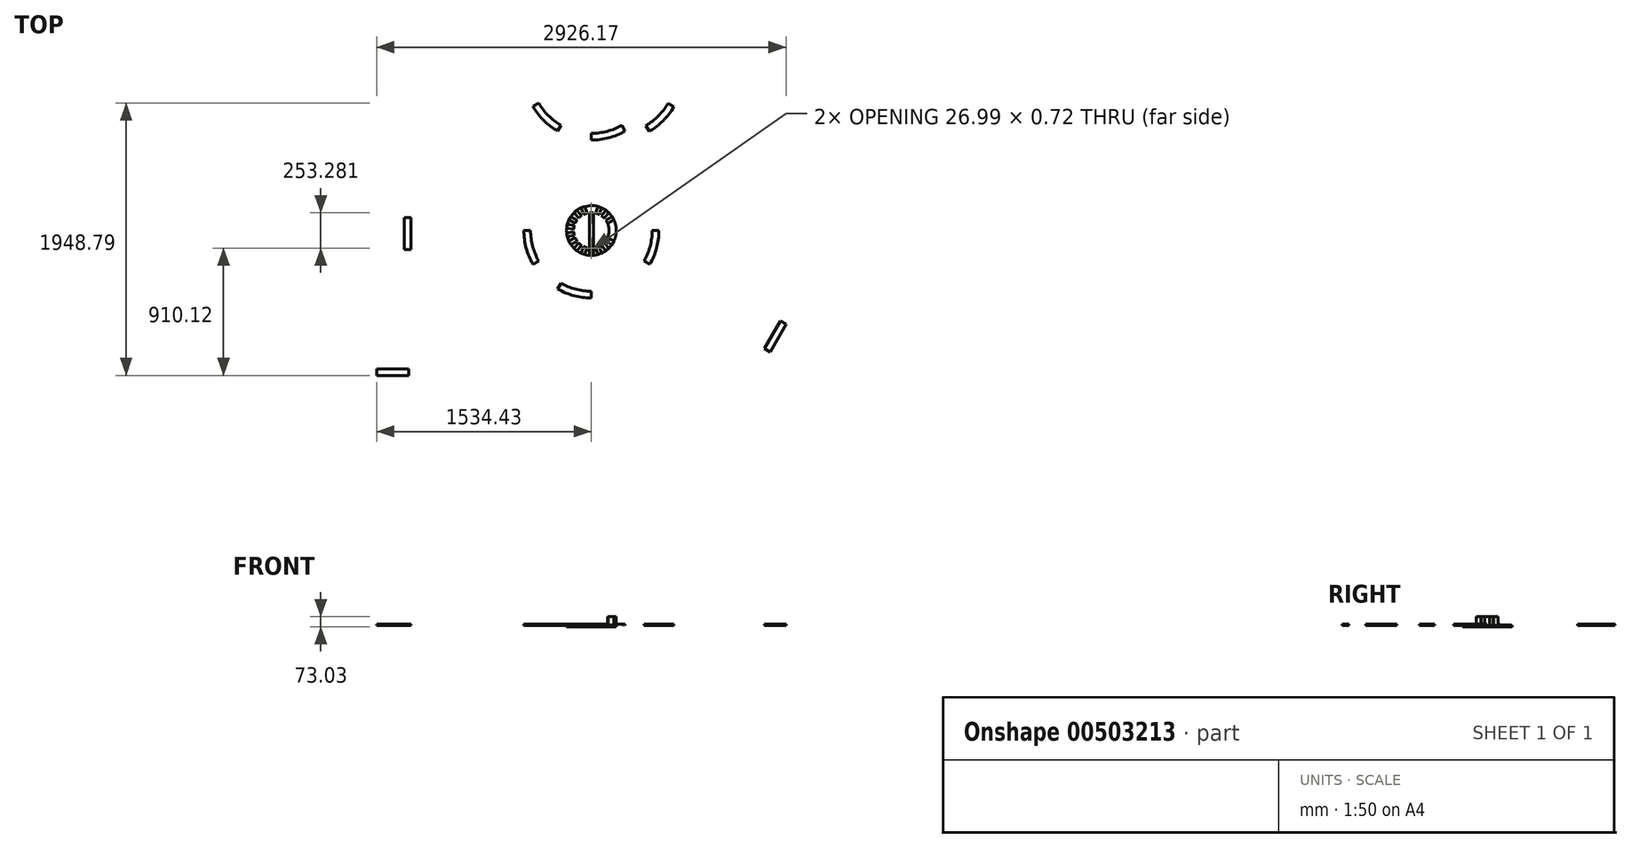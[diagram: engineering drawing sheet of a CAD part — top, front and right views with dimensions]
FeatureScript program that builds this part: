
annotation { "Feature Type Name" : "Feature", "Feature Type Description" : "" }
export const myFeature = defineFeature(function(context is Context, id is Id, definition is map)
    precondition{}
    {
        {
            var Q0;
            Q0=qCreatedBy(makeId("Top.planeOp"),FACE);
            var sketch = newSketch(context, id + "F0", { "sketchPlane" : qUnion([Q0])});
            skArc(sketch, "E0", {"start": v(-482.6, 0) * mm, "mid": v(-466.16, -124.9) * mm, "end": v(-417.94, -241.3) * mm});
            skArc(sketch, "E1.0", {"start": v(-434.98, 0) * mm, "mid": v(-420.15, -112.58) * mm, "end": v(-376.7, -217.49) * mm});
            skLineSegment(sketch, "E2", {"start": v(-482.6, 0) * mm, "end": v(-434.98, 0) * mm});
            skLineSegment(sketch, "E3", {"start": v(0, -434.98) * mm, "end": v(0, -482.6) * mm});
            skLineSegment(sketch, "E4", {"start": v(-376.7, -217.49) * mm, "end": v(-417.94, -241.3) * mm});
            skLineSegment(sketch, "E5", {"start": v(-217.49, -376.7) * mm, "end": v(-241.3, -417.94) * mm});
            skLineSegment(sketch, "E6.MirrorCS", {"start": v(376.7, -217.49) * mm, "end": v(417.94, -241.3) * mm});
            skLineSegment(sketch, "E7.MirrorCS", {"start": v(482.6, 0) * mm, "end": v(434.98, 0) * mm});
            skArc(sketch, "E8.MirrorCS", {"start": v(434.98, 0) * mm, "mid": v(420.15, -112.58) * mm, "end": v(376.7, -217.49) * mm});
            skArc(sketch, "E9.MirrorCS", {"start": v(482.6, 0) * mm, "mid": v(466.16, -124.9) * mm, "end": v(417.94, -241.3) * mm});
            skArc(sketch, "E10.trimOffspring", {"start": v(-217.49, -376.7) * mm, "mid": v(-112.58, -420.15) * mm, "end": v(0, -434.98) * mm});
            skArc(sketch, "E11.trimOffspring", {"start": v(-241.3, -417.94) * mm, "mid": v(-124.9, -466.16) * mm, "end": v(0, -482.6) * mm});
            skPoint(sketch, "E12.trimOffspring.end.orphan", {"position": v(0, -482.6) * mm});
            skPoint(sketch, "E13.MirrorCS.end.orphan", {"position": v(241.3, -417.94) * mm});
            skSolve(sketch);
        }
        {
            var Q0;
            Q0=qCreatedBy(makeId("Top.planeOp"),FACE);
            var sketch = newSketch(context, id + "F1", { "sketchPlane" : qUnion([Q0])});
            skArc(sketch, "E14", {"start": v(-417.94, 888.21) * mm, "mid": v(-341.25, 788.26) * mm, "end": v(-241.3, 711.57) * mm});
            skArc(sketch, "E15.0", {"start": v(-376.7, 912.03) * mm, "mid": v(-307.57, 821.94) * mm, "end": v(-217.49, 752.81) * mm});
            skLineSegment(sketch, "E16", {"start": v(-376.7, 912.03) * mm, "end": v(-417.94, 888.21) * mm});
            skLineSegment(sketch, "E17", {"start": v(-417.94, 888.21) * mm, "end": v(-376.7, 912.03) * mm});
            skLineSegment(sketch, "E18", {"start": v(-217.49, 752.81) * mm, "end": v(-241.3, 711.57) * mm});
            skLineSegment(sketch, "E19", {"start": v(217.49, 752.81) * mm, "end": v(241.3, 711.57) * mm});
            skLineSegment(sketch, "E20", {"start": v(241.3, 711.57) * mm, "end": v(217.49, 752.81) * mm});
            skArc(sketch, "E21.trimOffspring", {"start": v(0, 694.54) * mm, "mid": v(112.58, 709.36) * mm, "end": v(217.49, 752.81) * mm});
            skArc(sketch, "E22.trimOffspring", {"start": v(0, 646.91) * mm, "mid": v(124.9, 663.36) * mm, "end": v(241.3, 711.57) * mm});
            skLineSegment(sketch, "E23", {"start": v(0, 694.54) * mm, "end": v(0, 646.91) * mm});
            skLineSegment(sketch, "E24", {"start": v(589.96, 885.7) * mm, "end": v(548.71, 909.5) * mm});
            skArc(sketch, "E25", {"start": v(413.31, 709.05) * mm, "mid": v(513.26, 785.74) * mm, "end": v(589.96, 885.7) * mm});
            skArc(sketch, "E26", {"start": v(389.5, 750.3) * mm, "mid": v(479.59, 819.42) * mm, "end": v(548.71, 909.5) * mm});
            skLineSegment(sketch, "E27", {"start": v(413.31, 709.05) * mm, "end": v(389.5, 750.3) * mm});
            skLineSegment(sketch, "E28.bottom", {"start": v(-1336.41, -137.19) * mm, "end": v(-1288.79, -137.19) * mm});
            skLineSegment(sketch, "E28.top", {"start": v(-1336.41, 91.41) * mm, "end": v(-1288.79, 91.41) * mm});
            skLineSegment(sketch, "E28.left", {"start": v(-1336.41, -137.19) * mm, "end": v(-1336.41, 91.41) * mm});
            skLineSegment(sketch, "E28.right", {"start": v(-1288.79, -137.19) * mm, "end": v(-1288.79, 91.41) * mm});
            skLineSegment(sketch, "E29.bottom", {"start": v(-1534.43, -1036.76) * mm, "end": v(-1305.83, -1036.76) * mm});
            skLineSegment(sketch, "E29.top", {"start": v(-1534.43, -989.13) * mm, "end": v(-1305.83, -989.13) * mm});
            skLineSegment(sketch, "E29.left", {"start": v(-1534.43, -1036.76) * mm, "end": v(-1534.43, -989.13) * mm});
            skLineSegment(sketch, "E29.right", {"start": v(-1305.83, -1036.76) * mm, "end": v(-1305.83, -989.13) * mm});
            skSolve(sketch);
        }
        {
            var Q0;
            Q0 = qSketchRegion(id + "F0", true);
            var Q1;
            Q1 = qSketchRegion(id + "F1", true);
            extrude(context, id + "F2", {"entities" : qUnion([Q0, Q1]), "depth" : 9.52 * mm});
        }
        {
            var Q0;
            Q0=qCreatedBy(makeId("Top.planeOp"),FACE);
            var sketch = newSketch(context, id + "F3", { "sketchPlane" : qUnion([Q0])});
            skLineSegment(sketch, "E30.bottom", {"start": v(1236.2, -844.46) * mm, "end": v(1277.44, -868.27) * mm});
            skLineSegment(sketch, "E30.top", {"start": v(1350.5, -646.48) * mm, "end": v(1391.74, -670.3) * mm});
            skLineSegment(sketch, "E30.left", {"start": v(1236.2, -844.46) * mm, "end": v(1350.5, -646.48) * mm});
            skLineSegment(sketch, "E30.right", {"start": v(1277.44, -868.27) * mm, "end": v(1391.74, -670.3) * mm});
            skSolve(sketch);
        }
        {
            var Q0;
            Q0 = qSketchRegion(id + "F3", true);
            extrude(context, id + "F4", {"entities" : qUnion([Q0]), "depth" : 9.52 * mm});
        }
        {
            var Q0;
            Q0=qCreatedBy(makeId("Top.planeOp"),FACE);
            var sketch = newSketch(context, id + "F5", { "sketchPlane" : qUnion([Q0])});
            skCircle(sketch, "E31", {"center": v(0, 0) * mm, "radius": 177.8 * mm});
            skCircle(sketch, "E32", {"center": v(0, 0) * mm, "radius": 127 * mm});
            skLineSegment(sketch, "E33.bottom", {"start": v(13.5, -177.29) * mm, "end": v(-13.5, -177.29) * mm});
            skLineSegment(sketch, "E33.top", {"start": v(13.5, 177.29) * mm, "end": v(-13.5, 177.29) * mm});
            skLineSegment(sketch, "E33.left", {"start": v(13.5, -177.29) * mm, "end": v(13.5, -126.28) * mm});
            skLineSegment(sketch, "E33.right", {"start": v(-13.5, -177.29) * mm, "end": v(-13.5, -126.28) * mm});
            skLineSegment(sketch, "E34.trimOffspring", {"start": v(-13.5, 126.28) * mm, "end": v(-13.5, 177.29) * mm});
            skLineSegment(sketch, "E35.trimOffspring", {"start": v(13.5, 126.28) * mm, "end": v(13.5, 177.29) * mm});
            skLineSegment(sketch, "E36.1.0", {"start": v(47.96, -171.21) * mm, "end": v(30.51, -123.28) * mm});
            skLineSegment(sketch, "E36.1.1", {"start": v(73.32, -161.98) * mm, "end": v(47.96, -171.21) * mm});
            skLineSegment(sketch, "E36.1.2", {"start": v(73.32, -161.98) * mm, "end": v(55.87, -114.05) * mm});
            skLineSegment(sketch, "E36.2.0", {"start": v(103.62, -144.48) * mm, "end": v(70.84, -105.41) * mm});
            skLineSegment(sketch, "E36.2.1", {"start": v(124.3, -127.14) * mm, "end": v(103.62, -144.48) * mm});
            skLineSegment(sketch, "E36.2.2", {"start": v(124.3, -127.14) * mm, "end": v(91.5, -88.06) * mm});
            skLineSegment(sketch, "E36.3.0", {"start": v(146.79, -100.33) * mm, "end": v(102.62, -74.83) * mm});
            skLineSegment(sketch, "E36.3.1", {"start": v(160.28, -76.96) * mm, "end": v(146.79, -100.33) * mm});
            skLineSegment(sketch, "E36.3.2", {"start": v(160.28, -76.96) * mm, "end": v(116.1, -51.45) * mm});
            skLineSegment(sketch, "E36.4.1", {"start": v(176.94, -17.5) * mm, "end": v(172.25, -44.07) * mm});
            skLineSegment(sketch, "E36.5.1", {"start": v(172.25, 44.07) * mm, "end": v(176.94, 17.5) * mm});
            skLineSegment(sketch, "E36.6.0", {"start": v(160.28, 76.96) * mm, "end": v(116.1, 51.45) * mm});
            skLineSegment(sketch, "E36.6.1", {"start": v(146.79, 100.33) * mm, "end": v(160.28, 76.96) * mm});
            skLineSegment(sketch, "E36.6.2", {"start": v(146.79, 100.33) * mm, "end": v(102.62, 74.83) * mm});
            skLineSegment(sketch, "E36.7.0", {"start": v(124.3, 127.14) * mm, "end": v(91.5, 88.06) * mm});
            skLineSegment(sketch, "E36.7.1", {"start": v(103.62, 144.48) * mm, "end": v(124.3, 127.14) * mm});
            skLineSegment(sketch, "E36.7.2", {"start": v(103.62, 144.48) * mm, "end": v(70.84, 105.41) * mm});
            skLineSegment(sketch, "E36.8.0", {"start": v(73.32, 161.98) * mm, "end": v(55.87, 114.05) * mm});
            skLineSegment(sketch, "E36.8.1", {"start": v(47.96, 171.21) * mm, "end": v(73.32, 161.98) * mm});
            skLineSegment(sketch, "E36.8.2", {"start": v(47.96, 171.21) * mm, "end": v(30.51, 123.28) * mm});
            skLineSegment(sketch, "E36.9.0", {"start": v(13.5, 177.29) * mm, "end": v(13.5, 126.28) * mm});
            skLineSegment(sketch, "E36.9.1", {"start": v(-13.5, 177.29) * mm, "end": v(13.5, 177.29) * mm});
            skLineSegment(sketch, "E36.9.2", {"start": v(-13.5, 177.29) * mm, "end": v(-13.5, 126.28) * mm});
            skLineSegment(sketch, "E36.10.0", {"start": v(-47.96, 171.21) * mm, "end": v(-30.51, 123.28) * mm});
            skLineSegment(sketch, "E36.10.1", {"start": v(-73.32, 161.98) * mm, "end": v(-47.96, 171.21) * mm});
            skLineSegment(sketch, "E36.10.2", {"start": v(-73.32, 161.98) * mm, "end": v(-55.87, 114.05) * mm});
            skLineSegment(sketch, "E36.11.0", {"start": v(-103.62, 144.48) * mm, "end": v(-70.84, 105.41) * mm});
            skLineSegment(sketch, "E36.11.1", {"start": v(-124.3, 127.14) * mm, "end": v(-103.62, 144.48) * mm});
            skLineSegment(sketch, "E36.11.2", {"start": v(-124.3, 127.14) * mm, "end": v(-91.5, 88.06) * mm});
            skLineSegment(sketch, "E36.12.0", {"start": v(-146.79, 100.33) * mm, "end": v(-102.62, 74.83) * mm});
            skLineSegment(sketch, "E36.12.1", {"start": v(-160.28, 76.96) * mm, "end": v(-146.79, 100.33) * mm});
            skLineSegment(sketch, "E36.12.2", {"start": v(-160.28, 76.96) * mm, "end": v(-116.1, 51.45) * mm});
            skLineSegment(sketch, "E36.13.0", {"start": v(-172.25, 44.07) * mm, "end": v(-122.02, 35.22) * mm});
            skLineSegment(sketch, "E36.13.1", {"start": v(-176.94, 17.5) * mm, "end": v(-172.25, 44.07) * mm});
            skLineSegment(sketch, "E36.13.2", {"start": v(-176.94, 17.5) * mm, "end": v(-126.7, 8.64) * mm});
            skLineSegment(sketch, "E36.14.0", {"start": v(-176.94, -17.5) * mm, "end": v(-126.7, -8.64) * mm});
            skLineSegment(sketch, "E36.14.1", {"start": v(-172.25, -44.07) * mm, "end": v(-176.94, -17.5) * mm});
            skLineSegment(sketch, "E36.14.2", {"start": v(-172.25, -44.07) * mm, "end": v(-122.02, -35.22) * mm});
            skLineSegment(sketch, "E36.15.0", {"start": v(-160.28, -76.96) * mm, "end": v(-116.1, -51.45) * mm});
            skLineSegment(sketch, "E36.15.1", {"start": v(-146.79, -100.33) * mm, "end": v(-160.28, -76.96) * mm});
            skLineSegment(sketch, "E36.15.2", {"start": v(-146.79, -100.33) * mm, "end": v(-102.62, -74.83) * mm});
            skLineSegment(sketch, "E36.16.0", {"start": v(-124.3, -127.14) * mm, "end": v(-91.5, -88.06) * mm});
            skLineSegment(sketch, "E36.16.1", {"start": v(-103.62, -144.48) * mm, "end": v(-124.3, -127.14) * mm});
            skLineSegment(sketch, "E36.16.2", {"start": v(-103.62, -144.48) * mm, "end": v(-70.84, -105.41) * mm});
            skLineSegment(sketch, "E36.17.0", {"start": v(-73.32, -161.98) * mm, "end": v(-55.87, -114.05) * mm});
            skLineSegment(sketch, "E36.17.1", {"start": v(-47.96, -171.21) * mm, "end": v(-73.32, -161.98) * mm});
            skLineSegment(sketch, "E36.17.2", {"start": v(-47.96, -171.21) * mm, "end": v(-30.51, -123.28) * mm});
            skLineSegment(sketch, "E37.bottom", {"start": v(13.5, -126.28) * mm, "end": v(-13.5, -126.28) * mm});
            skLineSegment(sketch, "E37.top", {"start": v(13.5, 126.28) * mm, "end": v(-13.5, 126.28) * mm});
            skLineSegment(sketch, "E37.left", {"start": v(13.5, -126.28) * mm, "end": v(13.5, 126.28) * mm});
            skLineSegment(sketch, "E37.right", {"start": v(-13.5, -126.28) * mm, "end": v(-13.5, 126.28) * mm});
            skSolve(sketch);
        }
        {
            var Q0;
            Q0 = qSketchRegion(id + "F5", true);
            var Q1;
            {var subQ3=sQuery(id+"F5.wireOp",EDGE,"E37.right");Q1=makeQuery(id+"F5.imprint","IMPRINT",FACE,{"disambiguationData":[TD([[makeQuery(id+"F5.imprint","IMPRINT",EDGE,{"derivedFrom":subQ3}),1.0]])]});}
            var Q2;
            {var subQ4=sQuery(id+"F5.wireOp",EDGE,"E37.left");Q2=makeQuery(id+"F5.imprint","IMPRINT",FACE,{"disambiguationData":[TD([[makeQuery(id+"F5.imprint","IMPRINT",EDGE,{"derivedFrom":subQ4}),-1.0]])]});}
            var Q3;
            Q3=makeQuery(id+"F5.imprint","IMPRINT",FACE,{"disambiguationData":[TD([[makeQuery(id+"F5.imprint","IMPRINT",EDGE,{"derivedFrom":sQuery(id+"F5.wireOp",EDGE,"E37.bottom")}),-1.0]])]});
            extrude(context, id + "F6", {"entities" : qUnion([Q0, Q1, Q2, Q3]), "oppositeDirection" : true, "depth" : 9.52 * mm});
        }
        {
            var Q0;
            {var subQ1=sQuery(id+"F5.wireOp",EDGE,"E36.9.0");Q0=makeQuery(id+"F5.imprint","IMPRINT",FACE,{"disambiguationData":[TD([[makeQuery(id+"F5.imprint","IMPRINT",EDGE,{"derivedFrom":subQ1}),-1.0]])]});}
            var Q1;
            Q1=makeQuery(id+"F5.imprint","IMPRINT",FACE,{"disambiguationData":[TD([[makeQuery(id+"F5.imprint","IMPRINT",EDGE,{"derivedFrom":sQuery(id+"F5.wireOp",EDGE,"E33.bottom")}),-1.0]])]});
            var Q2;
            {var subQ0=sQuery(id+"F5.wireOp",EDGE,"E36.1.0");Q2=makeQuery(id+"F5.imprint","IMPRINT",FACE,{"disambiguationData":[TD([[makeQuery(id+"F5.imprint","IMPRINT",EDGE,{"derivedFrom":subQ0}),-1.0]])]});}
            var Q3;
            {var subQ0=sQuery(id+"F5.wireOp",EDGE,"E36.2.0");Q3=makeQuery(id+"F5.imprint","IMPRINT",FACE,{"disambiguationData":[TD([[makeQuery(id+"F5.imprint","IMPRINT",EDGE,{"derivedFrom":subQ0}),-1.0]])]});}
            var Q4;
            {var subQ0=sQuery(id+"F5.wireOp",EDGE,"E36.3.0");Q4=makeQuery(id+"F5.imprint","IMPRINT",FACE,{"disambiguationData":[TD([[makeQuery(id+"F5.imprint","IMPRINT",EDGE,{"derivedFrom":subQ0}),-1.0]])]});}
            var Q5;
            {var subQ0=sQuery(id+"F5.wireOp",EDGE,"E36.6.0");Q5=makeQuery(id+"F5.imprint","IMPRINT",FACE,{"disambiguationData":[TD([[makeQuery(id+"F5.imprint","IMPRINT",EDGE,{"derivedFrom":subQ0}),-1.0]])]});}
            var Q6;
            {var subQ0=sQuery(id+"F5.wireOp",EDGE,"E36.7.0");Q6=makeQuery(id+"F5.imprint","IMPRINT",FACE,{"disambiguationData":[TD([[makeQuery(id+"F5.imprint","IMPRINT",EDGE,{"derivedFrom":subQ0}),-1.0]])]});}
            var Q7;
            {var subQ0=sQuery(id+"F5.wireOp",EDGE,"E36.8.0");Q7=makeQuery(id+"F5.imprint","IMPRINT",FACE,{"disambiguationData":[TD([[makeQuery(id+"F5.imprint","IMPRINT",EDGE,{"derivedFrom":subQ0}),-1.0]])]});}
            var Q8;
            {var subQ0=sQuery(id+"F5.wireOp",EDGE,"E36.10.0");Q8=makeQuery(id+"F5.imprint","IMPRINT",FACE,{"disambiguationData":[TD([[makeQuery(id+"F5.imprint","IMPRINT",EDGE,{"derivedFrom":subQ0}),-1.0]])]});}
            var Q9;
            {var subQ0=sQuery(id+"F5.wireOp",EDGE,"E36.11.0");Q9=makeQuery(id+"F5.imprint","IMPRINT",FACE,{"disambiguationData":[TD([[makeQuery(id+"F5.imprint","IMPRINT",EDGE,{"derivedFrom":subQ0}),-1.0]])]});}
            var Q10;
            {var subQ0=sQuery(id+"F5.wireOp",EDGE,"E36.12.0");Q10=makeQuery(id+"F5.imprint","IMPRINT",FACE,{"disambiguationData":[TD([[makeQuery(id+"F5.imprint","IMPRINT",EDGE,{"derivedFrom":subQ0}),-1.0]])]});}
            var Q11;
            {var subQ0=sQuery(id+"F5.wireOp",EDGE,"E36.13.0");Q11=makeQuery(id+"F5.imprint","IMPRINT",FACE,{"disambiguationData":[TD([[makeQuery(id+"F5.imprint","IMPRINT",EDGE,{"derivedFrom":subQ0}),-1.0]])]});}
            var Q12;
            {var subQ0=sQuery(id+"F5.wireOp",EDGE,"E36.14.0");Q12=makeQuery(id+"F5.imprint","IMPRINT",FACE,{"disambiguationData":[TD([[makeQuery(id+"F5.imprint","IMPRINT",EDGE,{"derivedFrom":subQ0}),-1.0]])]});}
            var Q13;
            {var subQ0=sQuery(id+"F5.wireOp",EDGE,"E36.15.0");Q13=makeQuery(id+"F5.imprint","IMPRINT",FACE,{"disambiguationData":[TD([[makeQuery(id+"F5.imprint","IMPRINT",EDGE,{"derivedFrom":subQ0}),-1.0]])]});}
            var Q14;
            {var subQ0=sQuery(id+"F5.wireOp",EDGE,"E36.16.0");Q14=makeQuery(id+"F5.imprint","IMPRINT",FACE,{"disambiguationData":[TD([[makeQuery(id+"F5.imprint","IMPRINT",EDGE,{"derivedFrom":subQ0}),-1.0]])]});}
            var Q15;
            {var subQ0=sQuery(id+"F5.wireOp",EDGE,"E36.17.0");Q15=makeQuery(id+"F5.imprint","IMPRINT",FACE,{"disambiguationData":[TD([[makeQuery(id+"F5.imprint","IMPRINT",EDGE,{"derivedFrom":subQ0}),-1.0]])]});}
            var Q16;
            Q16=makeQuery(id+"F5.imprint","IMPRINT",FACE,{"disambiguationData":[TD([[makeQuery(id+"F5.imprint","IMPRINT",EDGE,{"derivedFrom":sQuery(id+"F5.wireOp",EDGE,"E37.bottom")}),-1.0]])]});
            extrude(context, id + "F7", {"entities" : qUnion([Q0, Q1, Q2, Q3, Q4, Q5, Q6, Q7, Q8, Q9, Q10, Q11, Q12, Q13, Q14, Q15, Q16]), "depth" : 1.59 * mm});
        }
        {
            var Q0;
            {var subQ0=sQuery(id+"F5.wireOp",EDGE,"E36.3.2");Q0=makeQuery(id+"F5.imprint","IMPRINT",FACE,{"disambiguationData":[TD([[makeQuery(id+"F5.imprint","IMPRINT",EDGE,{"derivedFrom":subQ0}),-1.0]])]});}
            extrude(context, id + "F8", {"entities" : qUnion([Q0]), "depth" : 63.5 * mm});
        }
    });
